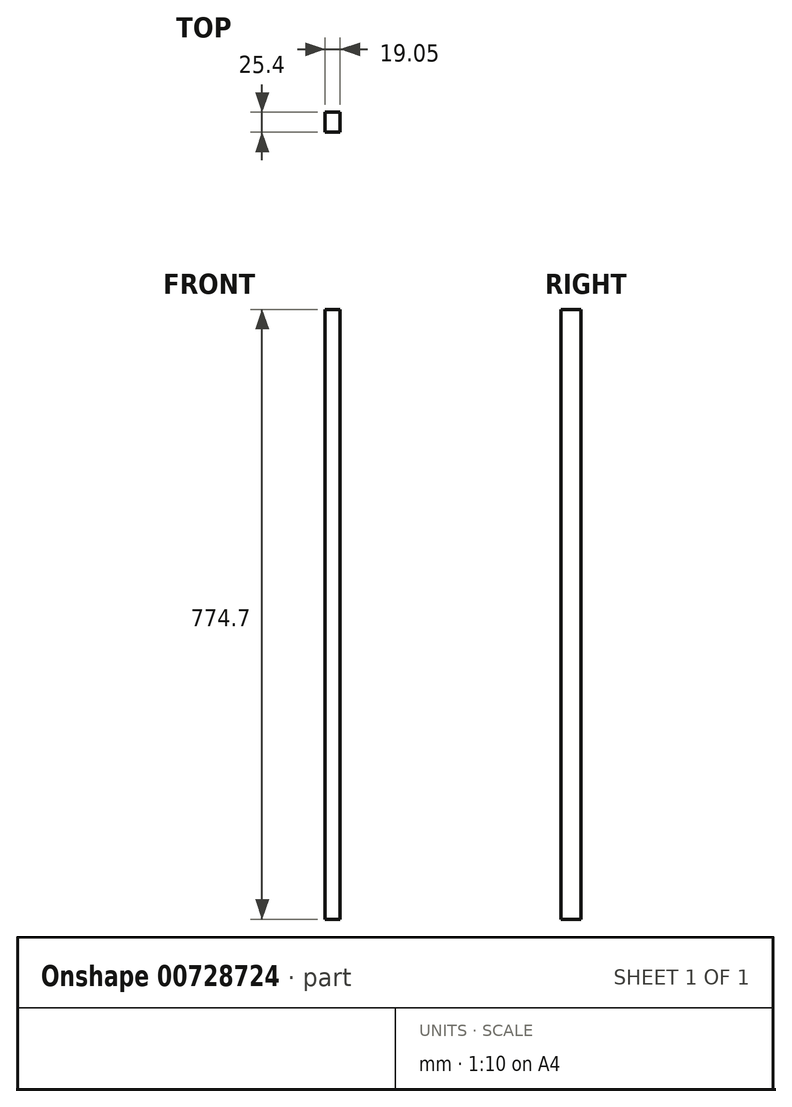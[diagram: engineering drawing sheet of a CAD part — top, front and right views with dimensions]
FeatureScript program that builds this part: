
annotation { "Feature Type Name" : "Feature", "Feature Type Description" : "" }
export const myFeature = defineFeature(function(context is Context, id is Id, definition is map)
    precondition{}
    {
        {
            var Q0;
            Q0=qCreatedBy(makeId("Right.planeOp"),FACE);
            var sketch = newSketch(context, id + "F0", { "sketchPlane" : qUnion([Q0])});
            skLineSegment(sketch, "E0.bottom", {"start": v(12.7, 387.35) * mm, "end": v(-12.7, 387.35) * mm});
            skLineSegment(sketch, "E0.top", {"start": v(12.7, -387.35) * mm, "end": v(-12.7, -387.35) * mm});
            skLineSegment(sketch, "E0.left", {"start": v(12.7, 387.35) * mm, "end": v(12.7, -387.35) * mm});
            skLineSegment(sketch, "E0.right", {"start": v(-12.7, 387.35) * mm, "end": v(-12.7, -387.35) * mm});
            skPoint(sketch, "E0.middle", {"position": v(0, 0) * mm});
            skSolve(sketch);
        }
        {
            var Q0;
            Q0 = qSketchRegion(id + "F0", true);
            extrude(context, id + "F1", {"entities" : qUnion([Q0]), "depth" : 19.05 * mm, "offsetDistance" : 25.4 * mm});
        }
    });
